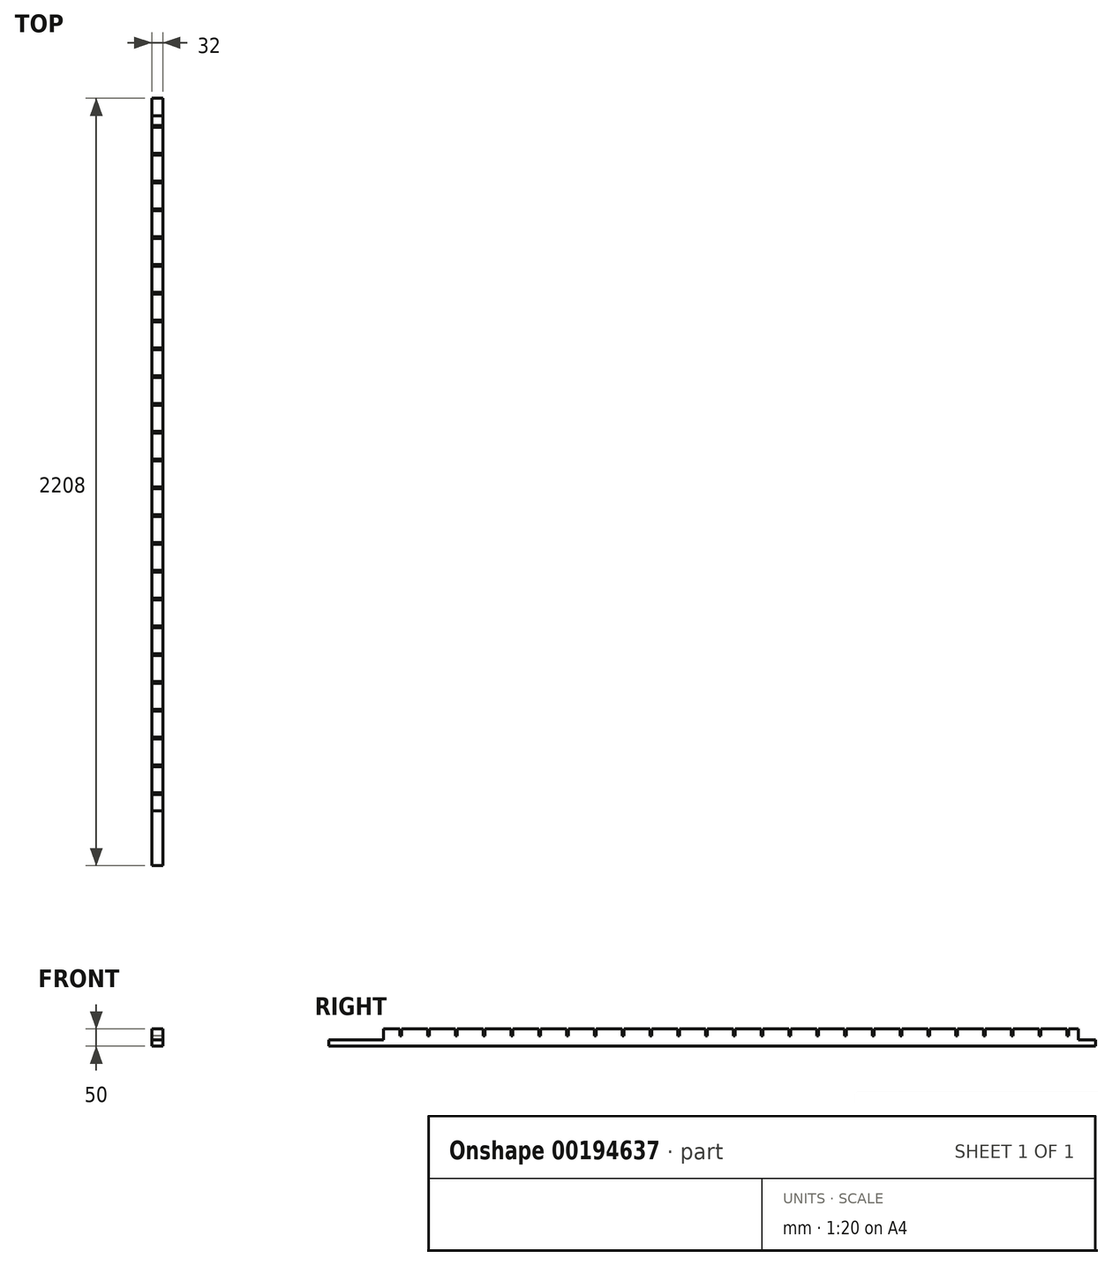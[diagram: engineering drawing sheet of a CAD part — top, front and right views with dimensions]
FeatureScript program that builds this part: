
annotation { "Feature Type Name" : "Feature", "Feature Type Description" : "" }
export const myFeature = defineFeature(function(context is Context, id is Id, definition is map)
    precondition{}
    {
        {
            var Q0;
            Q0=qCreatedBy(makeId("Front.planeOp"),FACE);
            var sketch = newSketch(context, id + "F0", { "sketchPlane" : qUnion([Q0])});
            skLineSegment(sketch, "E0.bottom", {"start": v(16, -9) * mm, "end": v(-16, -9) * mm});
            skLineSegment(sketch, "E0.top", {"start": v(16, 9) * mm, "end": v(-16, 9) * mm});
            skLineSegment(sketch, "E0.left", {"start": v(16, -9) * mm, "end": v(16, 9) * mm});
            skLineSegment(sketch, "E0.right", {"start": v(-16, -9) * mm, "end": v(-16, 9) * mm});
            skPoint(sketch, "E0.middle", {"position": v(0, 0) * mm});
            skSolve(sketch);
        }
        {
            var Q0;
            Q0 = qSketchRegion(id + "F0", true);
            extrude(context, id + "F1", {"entities" : qUnion([Q0]), "depth" : 2208 * mm});
        }
        {
            var Q0;
            Q0=qCreatedBy(makeId("Front.planeOp"),FACE);
            cPlane(context, id + "F2", {"entities" : qUnion([Q0]), "cplaneType" : CPlaneType.OFFSET, "offset" : 50 * mm, "width" : 150 * mm, "height" : 150 * mm});
        }
        {
            var Q0;
            Q0=qCreatedBy(id+"F2.planeOp",FACE);
            var sketch = newSketch(context, id + "F3", { "sketchPlane" : qUnion([Q0])});
            skLineSegment(sketch, "E1.bottom", {"start": v(16, 9) * mm, "end": v(-16, 9) * mm});
            skLineSegment(sketch, "E1.top", {"start": v(16, 41) * mm, "end": v(-16, 41) * mm});
            skLineSegment(sketch, "E1.left", {"start": v(16, 9) * mm, "end": v(16, 41) * mm});
            skLineSegment(sketch, "E1.right", {"start": v(-16, 9) * mm, "end": v(-16, 41) * mm});
            skPoint(sketch, "E1.middle", {"position": v(0, 25) * mm});
            skSolve(sketch);
        }
        {
            var Q0;
            Q0=makeQuery(id+"F3.imprint","IMPRINT",FACE,{"disambiguationData":[TD([[makeQuery(id+"F3.imprint","IMPRINT",EDGE,{"derivedFrom":sQuery(id+"F3.wireOp",EDGE,"E1.bottom")}),-1.0]])]});
            extrude(context, id + "F4", {"entities" : qUnion([Q0]), "operationType" : NewBodyOperationType.ADD, "depth" : 2000 * mm});
        }
        {
            var Q0;
            Q0=makeQuery(id+"F4.opExtrude","SWEPT_FACE",FACE,{"disambiguationData":[OSD([sQuery(id+"F3.wireOp",EDGE,"E1.right")])]});
            var sketch = newSketch(context, id + "F5", { "sketchPlane" : qUnion([Q0])});
            skLineSegment(sketch, "E2.0", {"start": v(83, 21) * mm, "end": v(83, 52) * mm});
            skLineSegment(sketch, "E3.0", {"start": v(78, 21) * mm, "end": v(78, 52) * mm});
            skLineSegment(sketch, "E4.0", {"start": v(83, 21) * mm, "end": v(78, 21) * mm});
            skLineSegment(sketch, "E5", {"start": v(78, 52) * mm, "end": v(83, 52) * mm});
            skLineSegment(sketch, "E6.1.0.0", {"start": v(163, 21) * mm, "end": v(163, 52) * mm});
            skLineSegment(sketch, "E6.1.0.1", {"start": v(158, 52) * mm, "end": v(163, 52) * mm});
            skLineSegment(sketch, "E6.1.0.2", {"start": v(158, 21) * mm, "end": v(158, 52) * mm});
            skLineSegment(sketch, "E6.1.0.3", {"start": v(163, 21) * mm, "end": v(158, 21) * mm});
            skLineSegment(sketch, "E6.2.0.0", {"start": v(243, 21) * mm, "end": v(243, 52) * mm});
            skLineSegment(sketch, "E6.2.0.1", {"start": v(238, 52) * mm, "end": v(243, 52) * mm});
            skLineSegment(sketch, "E6.2.0.2", {"start": v(238, 21) * mm, "end": v(238, 52) * mm});
            skLineSegment(sketch, "E6.2.0.3", {"start": v(243, 21) * mm, "end": v(238, 21) * mm});
            skLineSegment(sketch, "E6.3.0.0", {"start": v(323, 21) * mm, "end": v(323, 52) * mm});
            skLineSegment(sketch, "E6.3.0.1", {"start": v(318, 52) * mm, "end": v(323, 52) * mm});
            skLineSegment(sketch, "E6.3.0.2", {"start": v(318, 21) * mm, "end": v(318, 52) * mm});
            skLineSegment(sketch, "E6.3.0.3", {"start": v(323, 21) * mm, "end": v(318, 21) * mm});
            skLineSegment(sketch, "E6.4.0.0", {"start": v(403, 21) * mm, "end": v(403, 52) * mm});
            skLineSegment(sketch, "E6.4.0.1", {"start": v(398, 52) * mm, "end": v(403, 52) * mm});
            skLineSegment(sketch, "E6.4.0.2", {"start": v(398, 21) * mm, "end": v(398, 52) * mm});
            skLineSegment(sketch, "E6.4.0.3", {"start": v(403, 21) * mm, "end": v(398, 21) * mm});
            skLineSegment(sketch, "E6.5.0.0", {"start": v(483, 21) * mm, "end": v(483, 52) * mm});
            skLineSegment(sketch, "E6.5.0.1", {"start": v(478, 52) * mm, "end": v(483, 52) * mm});
            skLineSegment(sketch, "E6.5.0.2", {"start": v(478, 21) * mm, "end": v(478, 52) * mm});
            skLineSegment(sketch, "E6.5.0.3", {"start": v(483, 21) * mm, "end": v(478, 21) * mm});
            skLineSegment(sketch, "E6.6.0.0", {"start": v(563, 21) * mm, "end": v(563, 52) * mm});
            skLineSegment(sketch, "E6.6.0.1", {"start": v(558, 52) * mm, "end": v(563, 52) * mm});
            skLineSegment(sketch, "E6.6.0.2", {"start": v(558, 21) * mm, "end": v(558, 52) * mm});
            skLineSegment(sketch, "E6.6.0.3", {"start": v(563, 21) * mm, "end": v(558, 21) * mm});
            skLineSegment(sketch, "E6.7.0.0", {"start": v(643, 21) * mm, "end": v(643, 52) * mm});
            skLineSegment(sketch, "E6.7.0.1", {"start": v(638, 52) * mm, "end": v(643, 52) * mm});
            skLineSegment(sketch, "E6.7.0.2", {"start": v(638, 21) * mm, "end": v(638, 52) * mm});
            skLineSegment(sketch, "E6.7.0.3", {"start": v(643, 21) * mm, "end": v(638, 21) * mm});
            skLineSegment(sketch, "E6.8.0.0", {"start": v(723, 21) * mm, "end": v(723, 52) * mm});
            skLineSegment(sketch, "E6.8.0.1", {"start": v(718, 52) * mm, "end": v(723, 52) * mm});
            skLineSegment(sketch, "E6.8.0.2", {"start": v(718, 21) * mm, "end": v(718, 52) * mm});
            skLineSegment(sketch, "E6.8.0.3", {"start": v(723, 21) * mm, "end": v(718, 21) * mm});
            skLineSegment(sketch, "E6.9.0.0", {"start": v(803, 21) * mm, "end": v(803, 52) * mm});
            skLineSegment(sketch, "E6.9.0.1", {"start": v(798, 52) * mm, "end": v(803, 52) * mm});
            skLineSegment(sketch, "E6.9.0.2", {"start": v(798, 21) * mm, "end": v(798, 52) * mm});
            skLineSegment(sketch, "E6.9.0.3", {"start": v(803, 21) * mm, "end": v(798, 21) * mm});
            skLineSegment(sketch, "E6.10.0.0", {"start": v(883, 21) * mm, "end": v(883, 52) * mm});
            skLineSegment(sketch, "E6.10.0.1", {"start": v(878, 52) * mm, "end": v(883, 52) * mm});
            skLineSegment(sketch, "E6.10.0.2", {"start": v(878, 21) * mm, "end": v(878, 52) * mm});
            skLineSegment(sketch, "E6.10.0.3", {"start": v(883, 21) * mm, "end": v(878, 21) * mm});
            skLineSegment(sketch, "E6.11.0.0", {"start": v(963, 21) * mm, "end": v(963, 52) * mm});
            skLineSegment(sketch, "E6.11.0.1", {"start": v(958, 52) * mm, "end": v(963, 52) * mm});
            skLineSegment(sketch, "E6.11.0.2", {"start": v(958, 21) * mm, "end": v(958, 52) * mm});
            skLineSegment(sketch, "E6.11.0.3", {"start": v(963, 21) * mm, "end": v(958, 21) * mm});
            skLineSegment(sketch, "E6.12.0.0", {"start": v(1043, 21) * mm, "end": v(1043, 52) * mm});
            skLineSegment(sketch, "E6.12.0.1", {"start": v(1038, 52) * mm, "end": v(1043, 52) * mm});
            skLineSegment(sketch, "E6.12.0.2", {"start": v(1038, 21) * mm, "end": v(1038, 52) * mm});
            skLineSegment(sketch, "E6.12.0.3", {"start": v(1043, 21) * mm, "end": v(1038, 21) * mm});
            skLineSegment(sketch, "E6.13.0.0", {"start": v(1123, 21) * mm, "end": v(1123, 52) * mm});
            skLineSegment(sketch, "E6.13.0.1", {"start": v(1118, 52) * mm, "end": v(1123, 52) * mm});
            skLineSegment(sketch, "E6.13.0.2", {"start": v(1118, 21) * mm, "end": v(1118, 52) * mm});
            skLineSegment(sketch, "E6.13.0.3", {"start": v(1123, 21) * mm, "end": v(1118, 21) * mm});
            skLineSegment(sketch, "E6.14.0.0", {"start": v(1203, 21) * mm, "end": v(1203, 52) * mm});
            skLineSegment(sketch, "E6.14.0.1", {"start": v(1198, 52) * mm, "end": v(1203, 52) * mm});
            skLineSegment(sketch, "E6.14.0.2", {"start": v(1198, 21) * mm, "end": v(1198, 52) * mm});
            skLineSegment(sketch, "E6.14.0.3", {"start": v(1203, 21) * mm, "end": v(1198, 21) * mm});
            skLineSegment(sketch, "E6.15.0.0", {"start": v(1283, 21) * mm, "end": v(1283, 52) * mm});
            skLineSegment(sketch, "E6.15.0.1", {"start": v(1278, 52) * mm, "end": v(1283, 52) * mm});
            skLineSegment(sketch, "E6.15.0.2", {"start": v(1278, 21) * mm, "end": v(1278, 52) * mm});
            skLineSegment(sketch, "E6.15.0.3", {"start": v(1283, 21) * mm, "end": v(1278, 21) * mm});
            skLineSegment(sketch, "E6.16.0.0", {"start": v(1363, 21) * mm, "end": v(1363, 52) * mm});
            skLineSegment(sketch, "E6.16.0.1", {"start": v(1358, 52) * mm, "end": v(1363, 52) * mm});
            skLineSegment(sketch, "E6.16.0.2", {"start": v(1358, 21) * mm, "end": v(1358, 52) * mm});
            skLineSegment(sketch, "E6.16.0.3", {"start": v(1363, 21) * mm, "end": v(1358, 21) * mm});
            skLineSegment(sketch, "E6.17.0.0", {"start": v(1443, 21) * mm, "end": v(1443, 52) * mm});
            skLineSegment(sketch, "E6.17.0.1", {"start": v(1438, 52) * mm, "end": v(1443, 52) * mm});
            skLineSegment(sketch, "E6.17.0.2", {"start": v(1438, 21) * mm, "end": v(1438, 52) * mm});
            skLineSegment(sketch, "E6.17.0.3", {"start": v(1443, 21) * mm, "end": v(1438, 21) * mm});
            skLineSegment(sketch, "E6.18.0.0", {"start": v(1523, 21) * mm, "end": v(1523, 52) * mm});
            skLineSegment(sketch, "E6.18.0.1", {"start": v(1518, 52) * mm, "end": v(1523, 52) * mm});
            skLineSegment(sketch, "E6.18.0.2", {"start": v(1518, 21) * mm, "end": v(1518, 52) * mm});
            skLineSegment(sketch, "E6.18.0.3", {"start": v(1523, 21) * mm, "end": v(1518, 21) * mm});
            skLineSegment(sketch, "E6.19.0.0", {"start": v(1603, 21) * mm, "end": v(1603, 52) * mm});
            skLineSegment(sketch, "E6.19.0.1", {"start": v(1598, 52) * mm, "end": v(1603, 52) * mm});
            skLineSegment(sketch, "E6.19.0.2", {"start": v(1598, 21) * mm, "end": v(1598, 52) * mm});
            skLineSegment(sketch, "E6.19.0.3", {"start": v(1603, 21) * mm, "end": v(1598, 21) * mm});
            skLineSegment(sketch, "E6.20.0.0", {"start": v(1683, 21) * mm, "end": v(1683, 52) * mm});
            skLineSegment(sketch, "E6.20.0.1", {"start": v(1678, 52) * mm, "end": v(1683, 52) * mm});
            skLineSegment(sketch, "E6.20.0.2", {"start": v(1678, 21) * mm, "end": v(1678, 52) * mm});
            skLineSegment(sketch, "E6.20.0.3", {"start": v(1683, 21) * mm, "end": v(1678, 21) * mm});
            skLineSegment(sketch, "E6.21.0.0", {"start": v(1763, 21) * mm, "end": v(1763, 52) * mm});
            skLineSegment(sketch, "E6.21.0.1", {"start": v(1758, 52) * mm, "end": v(1763, 52) * mm});
            skLineSegment(sketch, "E6.21.0.2", {"start": v(1758, 21) * mm, "end": v(1758, 52) * mm});
            skLineSegment(sketch, "E6.21.0.3", {"start": v(1763, 21) * mm, "end": v(1758, 21) * mm});
            skLineSegment(sketch, "E6.22.0.0", {"start": v(1843, 21) * mm, "end": v(1843, 52) * mm});
            skLineSegment(sketch, "E6.22.0.1", {"start": v(1838, 52) * mm, "end": v(1843, 52) * mm});
            skLineSegment(sketch, "E6.22.0.2", {"start": v(1838, 21) * mm, "end": v(1838, 52) * mm});
            skLineSegment(sketch, "E6.22.0.3", {"start": v(1843, 21) * mm, "end": v(1838, 21) * mm});
            skLineSegment(sketch, "E6.23.0.0", {"start": v(1923, 21) * mm, "end": v(1923, 52) * mm});
            skLineSegment(sketch, "E6.23.0.1", {"start": v(1918, 52) * mm, "end": v(1923, 52) * mm});
            skLineSegment(sketch, "E6.23.0.2", {"start": v(1918, 21) * mm, "end": v(1918, 52) * mm});
            skLineSegment(sketch, "E6.23.0.3", {"start": v(1923, 21) * mm, "end": v(1918, 21) * mm});
            skLineSegment(sketch, "E6.24.0.0", {"start": v(2003, 21) * mm, "end": v(2003, 52) * mm});
            skLineSegment(sketch, "E6.24.0.1", {"start": v(1998, 52) * mm, "end": v(2003, 52) * mm});
            skLineSegment(sketch, "E6.24.0.2", {"start": v(1998, 21) * mm, "end": v(1998, 52) * mm});
            skLineSegment(sketch, "E6.24.0.3", {"start": v(2003, 21) * mm, "end": v(1998, 21) * mm});
            skLineSegment(sketch, "E6.direction1", {"start": v(83, 21) * mm, "end": v(163, 21) * mm, "construction": true});
            skSolve(sketch);
        }
        {
            var Q0;
            Q0 = qSketchRegion(id + "F5", true);
            extrude(context, id + "F6", {"entities" : qUnion([Q0]), "operationType" : NewBodyOperationType.REMOVE, "oppositeDirection" : true, "depth" : 32 * mm});
        }
    });
